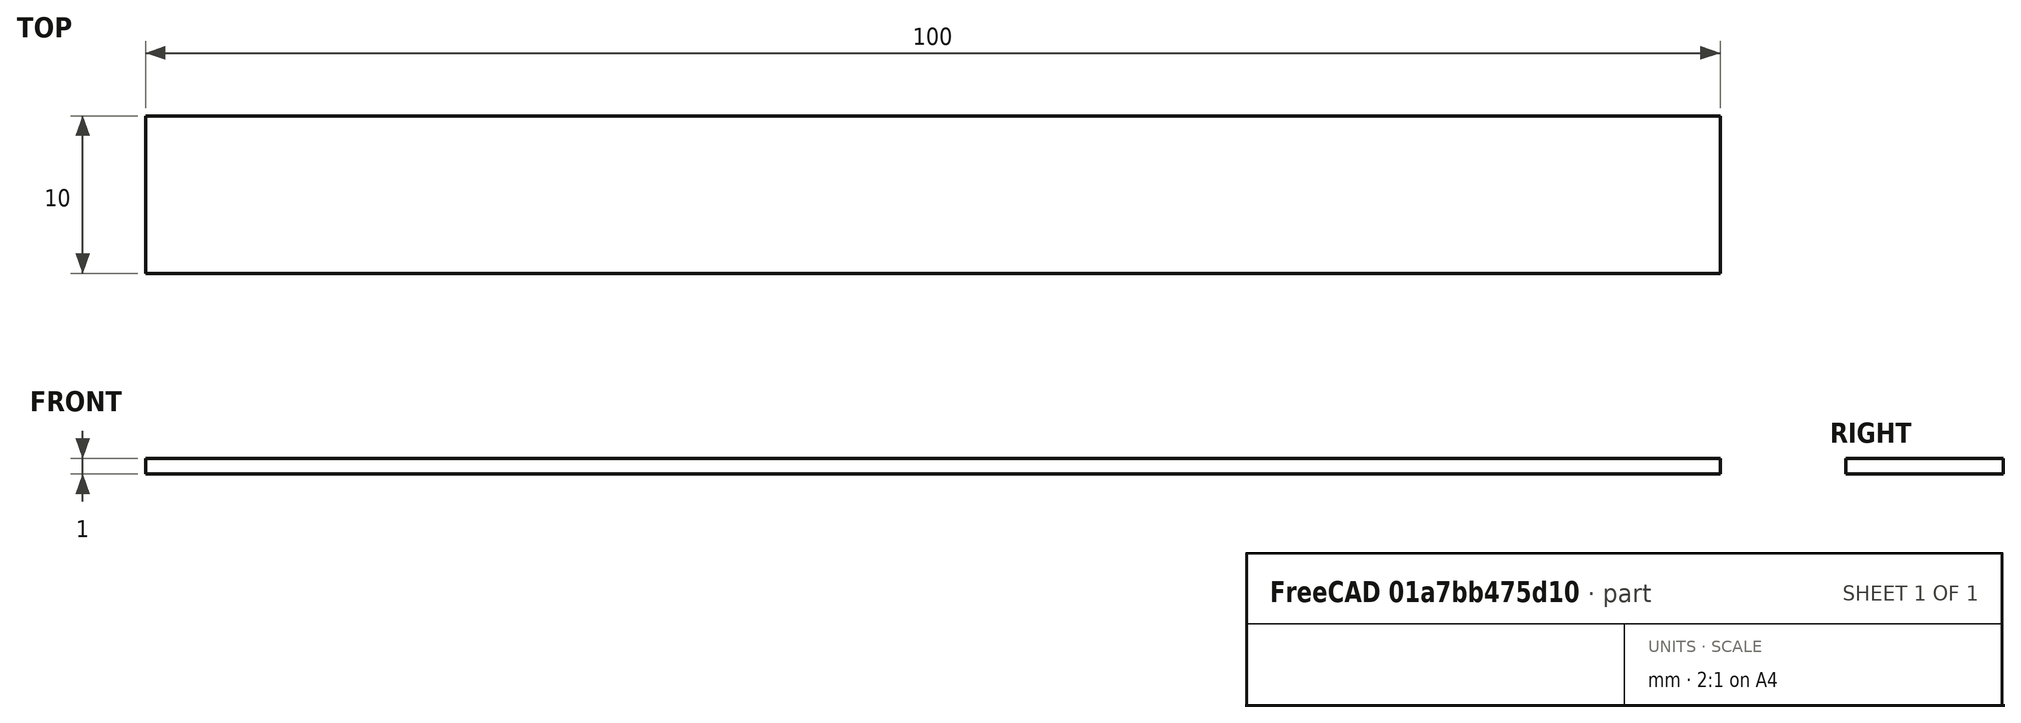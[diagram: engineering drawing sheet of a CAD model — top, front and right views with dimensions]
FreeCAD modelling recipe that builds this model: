
FCSTD DOCUMENT  (FreeCAD 1.0R39109 (Git))
Label: cantilever
License: All rights reserved
LicenseURL: http://en.wikipedia.org/wiki/All_rights_reserved
objects: Part::Box×1, Fem::ConstraintFixed×1, Fem::ConstraintForce×1, Fem::FemMeshShapeNetgenObject×1, Fem::FemSolverObjectPython×1, App::MaterialObjectPython×1, Fem::FemAnalysis×1
note: 1 computed .brp shape members not serialized (recipe doc carries the construction recipe); baked Part::Feature solids carry a one-line shape summary decoded from their .brp

FEATURE [Part::Box] Box  label="Cube"
  AttacherType = Attacher::AttachEngine3D
  Height = 1
  Length = 100
  Width = 10
FEATURE [Fem::ConstraintFixed] ConstraintFixed
  NormalDirection = (-1,0,0)
  Normals = (9) [(-1,0,0),(-1,0,0),(-1,0,0),(-1,0,0),(-1,0,0),(-1,0,0),(-1,0,0),(-1,0,0),(-1,0,0)]
  Points = (9) [(0,10,0),(0,10,0.5),(0,10,1),(0,5,0),(0,5,0.5),(0,5,1),(0,0,0),(0,0,0.5),(0,0,1)]
  References = -> [Box]
  Suppressed = false
FEATURE [Fem::ConstraintForce] ConstraintForce
  Direction = -> Box [Edge5]
  DirectionVector = (0,0,-1)
  Force = 1000
  NormalDirection = (1,0,0)
  Normals = (9) [(1,0,0),(1,0,0),(1,0,0),(1,0,0),(1,0,0),(1,0,0),(1,0,0),(1,0,0),(1,0,0)]
  Points = (9) [(100,10,0),(100,10,0.5),(100,10,1),(100,5,0),(100,5,0.5),(100,5,1),(100,0,0),(100,0,0.5),(100,0,1)]
  References = -> [Box]
  Reversed = true
  Suppressed = false
FEATURE [Fem::FemMeshShapeNetgenObject] FEMMeshNetgen
  Fineness = 2
  GrowthRate = 0.3
  MaxSize = 0
  MinSize = 10
  NbSegsPerEdge = 1
  NbSegsPerRadius = 2
  Optimize = true
  SecondOrder = true
  Shape = -> Box
FEATURE [Fem::FemSolverObjectPython] SolverCcxTools  # FEM object (typed FeaturePython)
  AnalysisType = 0
  BeamReducedIntegration = true
  BeamShellResultOutput3D = true
  BucklingFactors = 1
  EigenmodeHighLimit = 1000000
  EigenmodeLowLimit = 0
  EigenmodesCount = 10
  GeometricalNonlinearity = 0
  IterationsControlParameterCutb = 0.25,0.5,0.75,0.85,,,1.5,
  IterationsControlParameterIter = 4,8,9,200,10,400,,200,,
  IterationsControlParameterTimeUse = false
  IterationsMaximum = 2000
  IterationsUserDefinedIncrementations = false
  IterationsUserDefinedTimeStepLength = false
  MaterialNonlinearity = 0
  MatrixSolverType = 0
  ModelSpace = 0
  OutputFrequency = 1
  SplitInputWriter = false
  ThermoMechSteadyState = true
  ThermoMechType = 0
  TimeEnd = 1
  TimeInitialStep = 0.01
  TimeMaximumStep = 1
  TimeMinimumStep = 1e-05
FEATURE [App::MaterialObjectPython] MaterialSolid  # material (typed FeaturePython)
  Category = 0
  Material = AmbientColor=(0.0020, 0.0020, 0.0020, 1.0); Author=Juergen Riegel; AuthorAndLicense=CC-BY-3.0; CardName=CalculiX-Steel; Density=7.9e-06 kg/mm^3; Description=Standard steel material for CalculiX sample calculations; DiffuseColor=(0.0000, 0.0000, 0.0000, 1.0); EmissiveColor=(0.0000, 0.0000, 0.0000, 1.0); Father=Metal; License=CC-BY-3.0; Name=CalculiX-Steel; PoissonRatio=0.3; Shininess=0.06; SpecificHeat=5.9e+08 mm^2/(s^2*K); SpecularColor=(0.9800, 0.9800, 0.9800, 1.0); ThermalConductivity=43000 mm*kg/(s^3*K); ThermalExpansionCoefficient=1.2e-05 1/K; Transparency=0; YoungsModulus=2.1e+08 kg/(mm*s^2)
  UUID = 92589471-a6cb-4bbc-b748-d425a17dea7d
FEATURE [Fem::FemAnalysis] Analysis
  Group = -> [ConstraintFixed,ConstraintForce,SolverCcxTools,MaterialSolid]
